# Revit family: Digital_Media-Honeywell-Amplifier-580242(43)
name_source: partatom
category: Electrical Equipment
revit_build: Autodesk Revit 2017 (Build: 20160225_1515(x64)
units: mm (PartAtom-declared; Revit-internal decimal feet)

## family parameters
Cut with Voids When Loaded = No
Host = Face
OmniClass Number = 23.85.50.00
OmniClass Title = Communication Systems
Part Type = Equipment Switch
Room Calculation Point = No
Round Connector Dimension = Use Diameter
Shared = No

## types (2) — shared parameters
Air Humidity = 0 ... 93 %
Ambient Temperature = -5 °C ... 55 °C
Apparent Load = 0 VA
Default Elevation = 1219 mm
Finish = Metal - Honeywell - Stainless Steel - Black
Frequency = 50 Hz
Load Sub-Classification = No
Manufacturer = Honeywell International
Manufacturer Fax Number = 02131/40615-606
Number of Poles = 1
Power Factor = 1
Product Documentation Link = https://www.esser-systems.com
Product Name = Four Channel Amplifier
Product Page URL = https://www.esser-systems.com
Rated Frequency = 50 ... 60 Hz (+10 % / -5 %)
Rated Load Current = 3 A
Rated Voltage = 230 V AC
Storage Temperature = -10 °C ... 55 °C
URL = www.esser-systems.com
Utility = No
Version = 2017 - v1.0a
Voltage = 230 V
Width = 483 mm

## per-type parameters (varying)
| type | Constraints | Depth | Description | Height | Model | Power Output | Rated current | Wattage | Watts | Weight |
| Four Channel amplifier 4XD250B - 580243 | 1 | 408 mm | Four channel amplifier 4XD250B | 90 mm | 580243 | 4 x 250 W | 2.95 A | 250 W | 250 W | 12.00 kgf |
| Four Channel amplifier 4XD125B - 580242 | 2 | 402 mm  [stored 1.3189 ft] | Four channel amplifier 4XD125B | 44 mm | 580242 | 4 x 125 W |  | 125 W | 125 W | 9.00 kgf |

note: [stored X ft] marks values corroborated as IEEE doubles in the binary element streams (Revit-internal decimal feet)

## geometry (parser evidence)
native form markers: Sweep x3
no freeform markers — native parametric forms only
